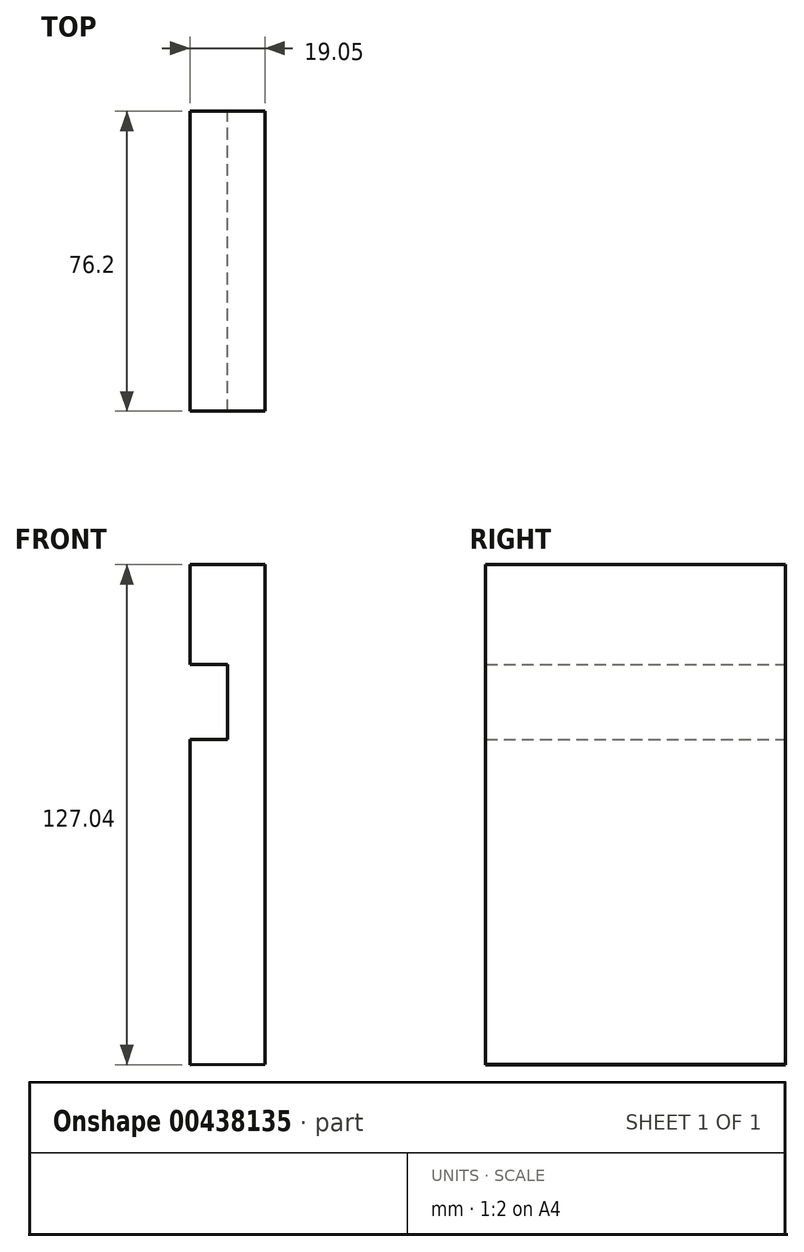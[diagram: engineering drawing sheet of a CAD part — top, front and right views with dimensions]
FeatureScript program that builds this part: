
annotation { "Feature Type Name" : "Feature", "Feature Type Description" : "" }
export const myFeature = defineFeature(function(context is Context, id is Id, definition is map)
    precondition{}
    {
        {
            var Q0;
            Q0=qCreatedBy(makeId("Front.planeOp"),FACE);
            var sketch = newSketch(context, id + "F0", { "sketchPlane" : qUnion([Q0])});
            skLineSegment(sketch, "E0", {"start": v(0, 73.14) * mm, "end": v(0, -53.86) * mm});
            skLineSegment(sketch, "E1", {"start": v(0, 73.14) * mm, "end": v(-19.05, 73.14) * mm});
            skLineSegment(sketch, "E2", {"start": v(-19.05, 73.14) * mm, "end": v(-19.05, 47.74) * mm});
            skLineSegment(sketch, "E3", {"start": v(-19.05, 47.74) * mm, "end": v(-9.52, 47.74) * mm});
            skLineSegment(sketch, "E4", {"start": v(-9.52, 47.74) * mm, "end": v(-9.52, 28.69) * mm});
            skLineSegment(sketch, "E5", {"start": v(-9.52, 28.69) * mm, "end": v(-19.05, 28.69) * mm});
            skLineSegment(sketch, "E6", {"start": v(-19.05, 28.69) * mm, "end": v(-19.05, -53.9) * mm});
            skLineSegment(sketch, "E7", {"start": v(0, -53.86) * mm, "end": v(-19.05, -53.9) * mm});
            skSolve(sketch);
        }
        {
            var Q0;
            Q0=makeQuery(id+"F0.imprint","IMPRINT",FACE,{"disambiguationData":[TD([[makeQuery(id+"F0.imprint","IMPRINT",EDGE,{"derivedFrom":sQuery(id+"F0.wireOp",EDGE,"E0")}),-1.0]])]});
            extrude(context, id + "F1", {"entities" : qUnion([Q0]), "depth" : 76.2 * mm});
        }
    });
